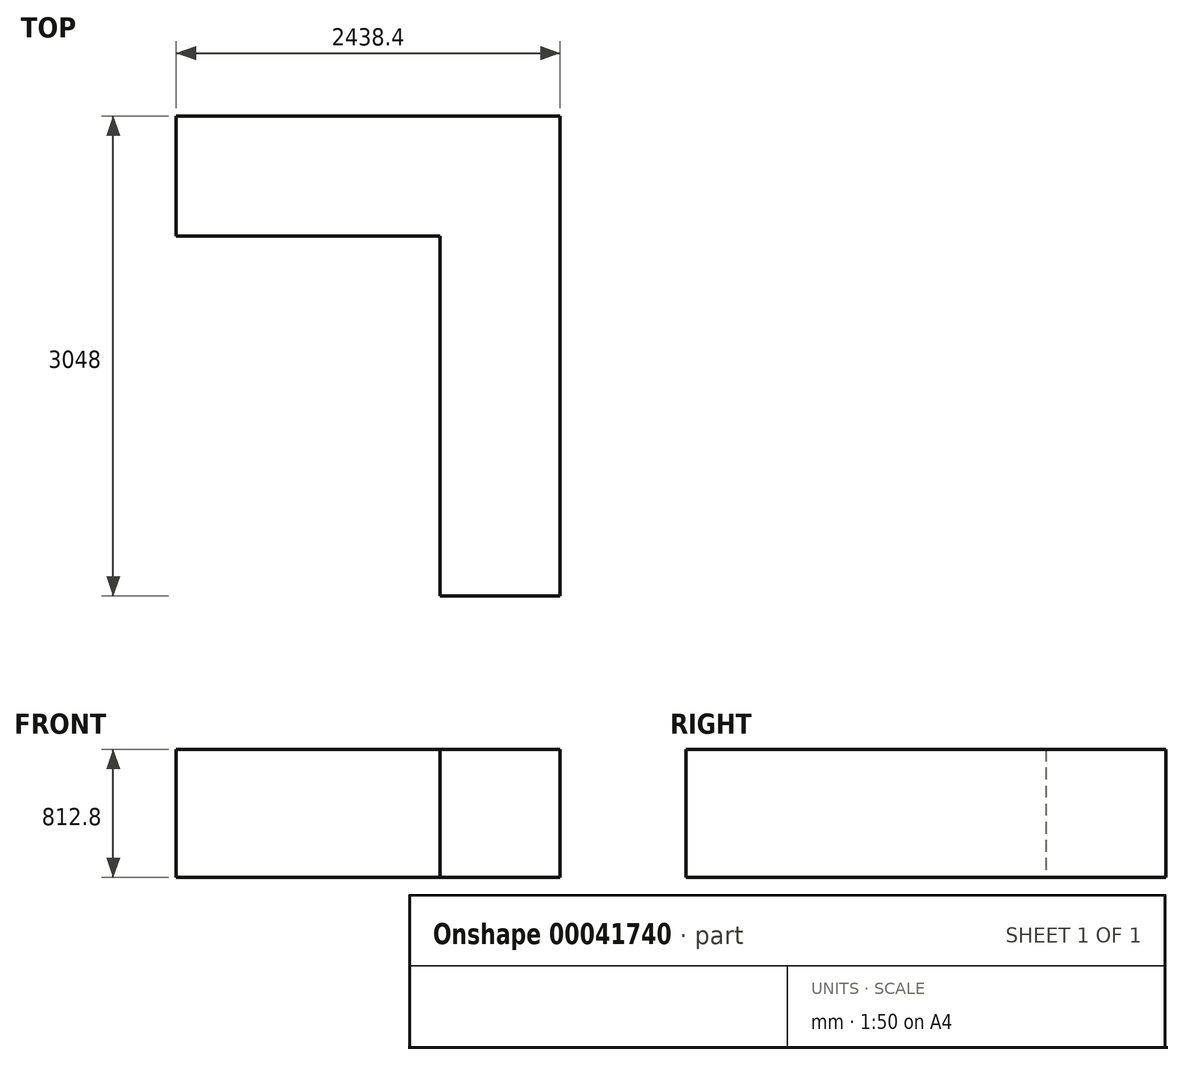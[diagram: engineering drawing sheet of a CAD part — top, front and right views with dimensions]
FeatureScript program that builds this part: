
annotation { "Feature Type Name" : "Feature", "Feature Type Description" : "" }
export const myFeature = defineFeature(function(context is Context, id is Id, definition is map)
    precondition{}
    {
        {
            var Q0;
            Q0=qCreatedBy(makeId("Top.planeOp"),FACE);
            var sketch = newSketch(context, id + "F0", { "sketchPlane" : qUnion([Q0])});
            skLineSegment(sketch, "E0.bottom", {"start": v(0, 0) * mm, "end": v(-2438.4, 0) * mm});
            skLineSegment(sketch, "E0.top", {"start": v(0, -762) * mm, "end": v(-2438.4, -762) * mm});
            skLineSegment(sketch, "E0.left", {"start": v(0, 0) * mm, "end": v(0, -762) * mm});
            skLineSegment(sketch, "E0.right", {"start": v(-2438.4, 0) * mm, "end": v(-2438.4, -762) * mm});
            skLineSegment(sketch, "E1.bottom", {"start": v(0, -762) * mm, "end": v(-762, -762) * mm});
            skLineSegment(sketch, "E1.top", {"start": v(0, -3048) * mm, "end": v(-762, -3048) * mm});
            skLineSegment(sketch, "E1.left", {"start": v(0, -762) * mm, "end": v(0, -3048) * mm});
            skLineSegment(sketch, "E1.right", {"start": v(-762, -762) * mm, "end": v(-762, -3048) * mm});
            skLineSegment(sketch, "E2.bottom", {"start": v(-762, -3048) * mm, "end": v(-2286, -3048) * mm});
            skLineSegment(sketch, "E2.top", {"start": v(-762, -2286) * mm, "end": v(-2286, -2286) * mm});
            skLineSegment(sketch, "E2.left", {"start": v(-762, -3048) * mm, "end": v(-762, -2286) * mm});
            skLineSegment(sketch, "E3", {"start": v(-2286, -2286) * mm, "end": v(-2286, -3048) * mm});
            skSolve(sketch);
        }
        {
            var Q0;
            Q0=makeQuery(id+"F0.imprint","IMPRINT",FACE,{"disambiguationData":[TD([[makeQuery(id+"F0.imprint","IMPRINT",EDGE,{"derivedFrom":sQuery(id+"F0.wireOp",EDGE,"E0.bottom")}),1.0]])]});
            var Q1;
            {var subQ1=sQuery(id+"F0.wireOp",EDGE,"E1.top");Q1=makeQuery(id+"F0.imprint","IMPRINT",FACE,{"disambiguationData":[TD([[makeQuery(id+"F0.imprint","IMPRINT",EDGE,{"derivedFrom":subQ1}),-1.0]])]});}
            extrude(context, id + "F1", {"entities" : qUnion([Q0, Q1]), "depth" : 812.8 * mm, "offsetDistance" : 30.48 * mm});
        }
    });
